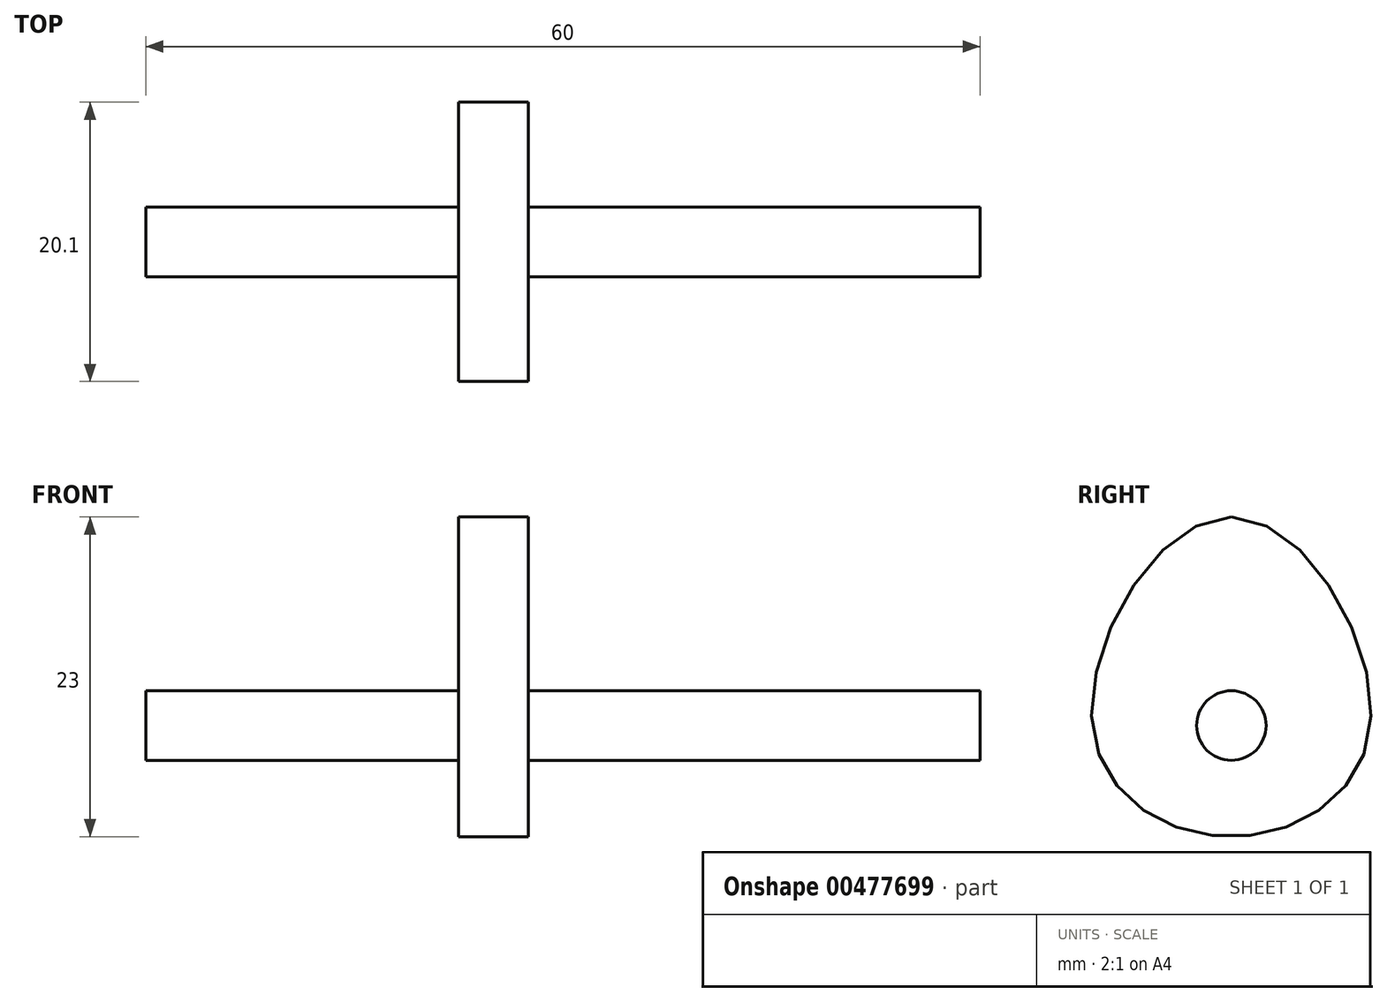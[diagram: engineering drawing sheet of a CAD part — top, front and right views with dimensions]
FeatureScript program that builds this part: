
annotation { "Feature Type Name" : "Feature", "Feature Type Description" : "" }
export const myFeature = defineFeature(function(context is Context, id is Id, definition is map)
    precondition{}
    {
        {
            var Q0;
            Q0=qCreatedBy(makeId("Right.planeOp"),FACE);
            var sketch = newSketch(context, id + "F0", { "sketchPlane" : qUnion([Q0])});
            skCircle(sketch, "E0", {"center": v(0, 0) * mm, "radius": 2.5 * mm});
            skFitSpline(sketch, "E1", {"points": [v(0, 15) * mm, v(-10, 0) * mm, v(0, -8) * mm, v(10, 0) * mm, v(0, 15) * mm]});
            skSolve(sketch);
        }
        {
            var Q0;
            Q0=makeQuery(id+"F0.imprint","IMPRINT",FACE,{"disambiguationData":[TD([[makeQuery(id+"F0.imprint","IMPRINT",EDGE,{"derivedFrom":sQuery(id+"F0.wireOp",EDGE,"E0")}),1.0]])]});
            extrude(context, id + "F1", {"entities" : qUnion([Q0]), "depth" : 35 * mm, "hasSecondDirection" : true, "secondDirectionOppositeDirection" : true, "secondDirectionDepth" : 25 * mm});
        }
        {
            var Q0;
            Q0=makeQuery(id+"F0.imprint","IMPRINT",FACE,{"disambiguationData":[TD([[makeQuery(id+"F0.imprint","IMPRINT",EDGE,{"derivedFrom":sQuery(id+"F0.wireOp",EDGE,"E0")}),-1.0]])]});
            extrude(context, id + "F2", {"entities" : qUnion([Q0]), "operationType" : NewBodyOperationType.ADD, "depth" : 2.5 * mm, "hasSecondDirection" : true, "secondDirectionOppositeDirection" : true, "secondDirectionDepth" : 2.5 * mm});
        }
    });
